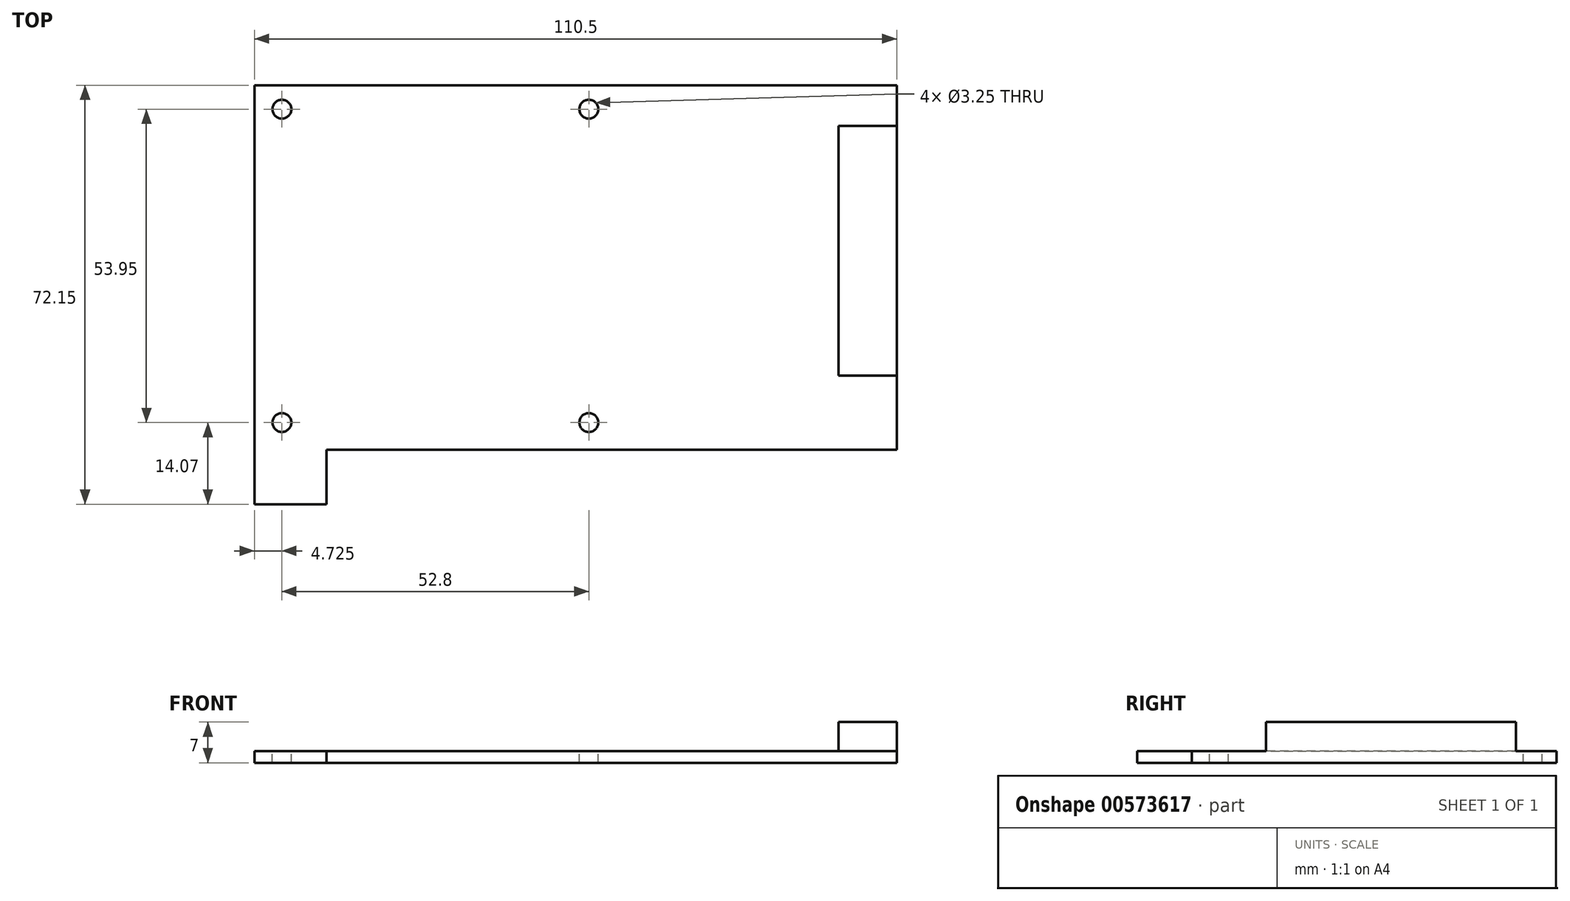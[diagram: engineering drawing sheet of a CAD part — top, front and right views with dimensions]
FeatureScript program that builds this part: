
annotation { "Feature Type Name" : "Feature", "Feature Type Description" : "" }
export const myFeature = defineFeature(function(context is Context, id is Id, definition is map)
    precondition{}
    {
        {
            var Q0;
            Q0=qCreatedBy(makeId("Top.planeOp"),FACE);
            var sketch = newSketch(context, id + "F0", { "sketchPlane" : qUnion([Q0])});
            skLineSegment(sketch, "E0.bottom", {"start": v(55.25, -31.37) * mm, "end": v(-55.25, -31.38) * mm});
            skLineSegment(sketch, "E0.top", {"start": v(55.25, 31.38) * mm, "end": v(-55.25, 31.37) * mm});
            skLineSegment(sketch, "E0.left", {"start": v(55.25, -31.37) * mm, "end": v(55.25, 31.38) * mm});
            skLineSegment(sketch, "E0.right", {"start": v(-55.25, -31.38) * mm, "end": v(-55.25, 31.37) * mm});
            skPoint(sketch, "E0.middle", {"position": v(0, 0) * mm});
            skSolve(sketch);
        }
        {
            var Q0;
            Q0 = qSketchRegion(id + "F0", true);
            extrude(context, id + "F1", {"entities" : qUnion([Q0]), "depth" : 2 * mm, "offsetDistance" : 25 * mm});
        }
        {
            var Q0;
            Q0=qCreatedBy(makeId("Top.planeOp"),FACE);
            var sketch = newSketch(context, id + "F2", { "sketchPlane" : qUnion([Q0])});
            skLineSegment(sketch, "E1.bottom", {"start": v(-55.25, -31.38) * mm, "end": v(-42.85, -31.38) * mm});
            skLineSegment(sketch, "E1.top", {"start": v(-55.25, -40.78) * mm, "end": v(-42.85, -40.78) * mm});
            skLineSegment(sketch, "E1.left", {"start": v(-55.25, -31.38) * mm, "end": v(-55.25, -40.78) * mm});
            skLineSegment(sketch, "E1.right", {"start": v(-42.85, -31.38) * mm, "end": v(-42.85, -40.78) * mm});
            skSolve(sketch);
        }
        {
            var Q0;
            Q0 = qSketchRegion(id + "F2", true);
            var Q1;
            Q1=makeQuery(id+"F1.opExtrude","CAP_FACE",FACE,{"disambiguationData":[OSD([sQuery(id+"F0.wireOp",EDGE,"E0.bottom"),sQuery(id+"F0.wireOp",EDGE,"E0.top"),sQuery(id+"F0.wireOp",EDGE,"E0.left"),sQuery(id+"F0.wireOp",EDGE,"E0.right")])],"isStart":false});
            extrude(context, id + "F3", {"entities" : qUnion([Q0]), "operationType" : NewBodyOperationType.ADD, "endBound" : BoundingType.UP_TO_SURFACE, "depth" : 25 * mm, "endBoundEntityFace" : qUnion([Q1]), "offsetDistance" : 25 * mm});
        }
        {
            var Q0;
            {var subQ0=sQuery(id+"F0.wireOp",EDGE,"E0.right");var subQ1=sQuery(id+"F0.wireOp",EDGE,"E0.left");var subQ2=sQuery(id+"F0.wireOp",EDGE,"E0.top");var subQ3=sQuery(id+"F0.wireOp",EDGE,"E0.bottom");Q0=makeQuery(id+"F3.boolean.opBoolean","MERGE",FACE,{"derivedFrom":[makeQuery(id+"F1.opExtrude","CAP_FACE",FACE,{"disambiguationData":[OSD([subQ3,subQ2,subQ1,subQ0])],"isStart":false}),makeQuery(id+"F3.opExtrude","CAP_FACE",FACE,{"disambiguationData":[OSD([subQ3,subQ2,subQ1,subQ0])],"isStart":false})]});}
            var sketch = newSketch(context, id + "F4", { "sketchPlane" : qUnion([Q0])});
            skLineSegment(sketch, "E2.bottom", {"start": v(-50.52, 27.25) * mm, "end": v(2.27, 27.25) * mm, "construction": true});
            skLineSegment(sketch, "E2.top", {"start": v(-50.52, -26.7) * mm, "end": v(2.27, -26.7) * mm, "construction": true});
            skLineSegment(sketch, "E2.left", {"start": v(-50.52, 27.25) * mm, "end": v(-50.52, -26.7) * mm, "construction": true});
            skLineSegment(sketch, "E2.right", {"start": v(2.27, 27.25) * mm, "end": v(2.28, -26.7) * mm, "construction": true});
            skCircle(sketch, "E3", {"center": v(-50.52, 27.25) * mm, "radius": 1.63 * mm});
            skCircle(sketch, "E4", {"center": v(2.27, 27.25) * mm, "radius": 1.63 * mm});
            skCircle(sketch, "E5", {"center": v(2.27, -26.7) * mm, "radius": 1.63 * mm});
            skCircle(sketch, "E6", {"center": v(-50.52, -26.7) * mm, "radius": 1.63 * mm});
            skSolve(sketch);
        }
        {
            var Q0;
            Q0 = qSketchRegion(id + "F4", true);
            extrude(context, id + "F5", {"entities" : qUnion([Q0]), "operationType" : NewBodyOperationType.REMOVE, "endBound" : BoundingType.THROUGH_ALL, "oppositeDirection" : true, "depth" : 25 * mm, "offsetDistance" : 25 * mm});
        }
        {
            var Q0;
            {var subQ0=sQuery(id+"F0.wireOp",EDGE,"E0.right");var subQ1=sQuery(id+"F0.wireOp",EDGE,"E0.left");var subQ2=sQuery(id+"F0.wireOp",EDGE,"E0.top");var subQ3=sQuery(id+"F0.wireOp",EDGE,"E0.bottom");Q0=makeQuery(id+"F3.boolean.opBoolean","MERGE",FACE,{"derivedFrom":[makeQuery(id+"F1.opExtrude","CAP_FACE",FACE,{"disambiguationData":[OSD([subQ3,subQ2,subQ1,subQ0])],"isStart":false}),makeQuery(id+"F3.opExtrude","CAP_FACE",FACE,{"disambiguationData":[OSD([subQ3,subQ2,subQ1,subQ0])],"isStart":false})]});}
            var sketch = newSketch(context, id + "F6", { "sketchPlane" : qUnion([Q0])});
            skLineSegment(sketch, "E7.bottom", {"start": v(55.25, 24.38) * mm, "end": v(45.25, 24.38) * mm});
            skLineSegment(sketch, "E7.top", {"start": v(55.25, -18.62) * mm, "end": v(45.25, -18.62) * mm});
            skLineSegment(sketch, "E7.left", {"start": v(55.25, 24.38) * mm, "end": v(55.25, -18.62) * mm});
            skLineSegment(sketch, "E7.right", {"start": v(45.25, 24.38) * mm, "end": v(45.25, -18.62) * mm});
            skSolve(sketch);
        }
        {
            var Q0;
            Q0 = qSketchRegion(id + "F6", true);
            extrude(context, id + "F7", {"entities" : qUnion([Q0]), "operationType" : NewBodyOperationType.ADD, "depth" : 5 * mm, "offsetDistance" : 25 * mm});
        }
    });
